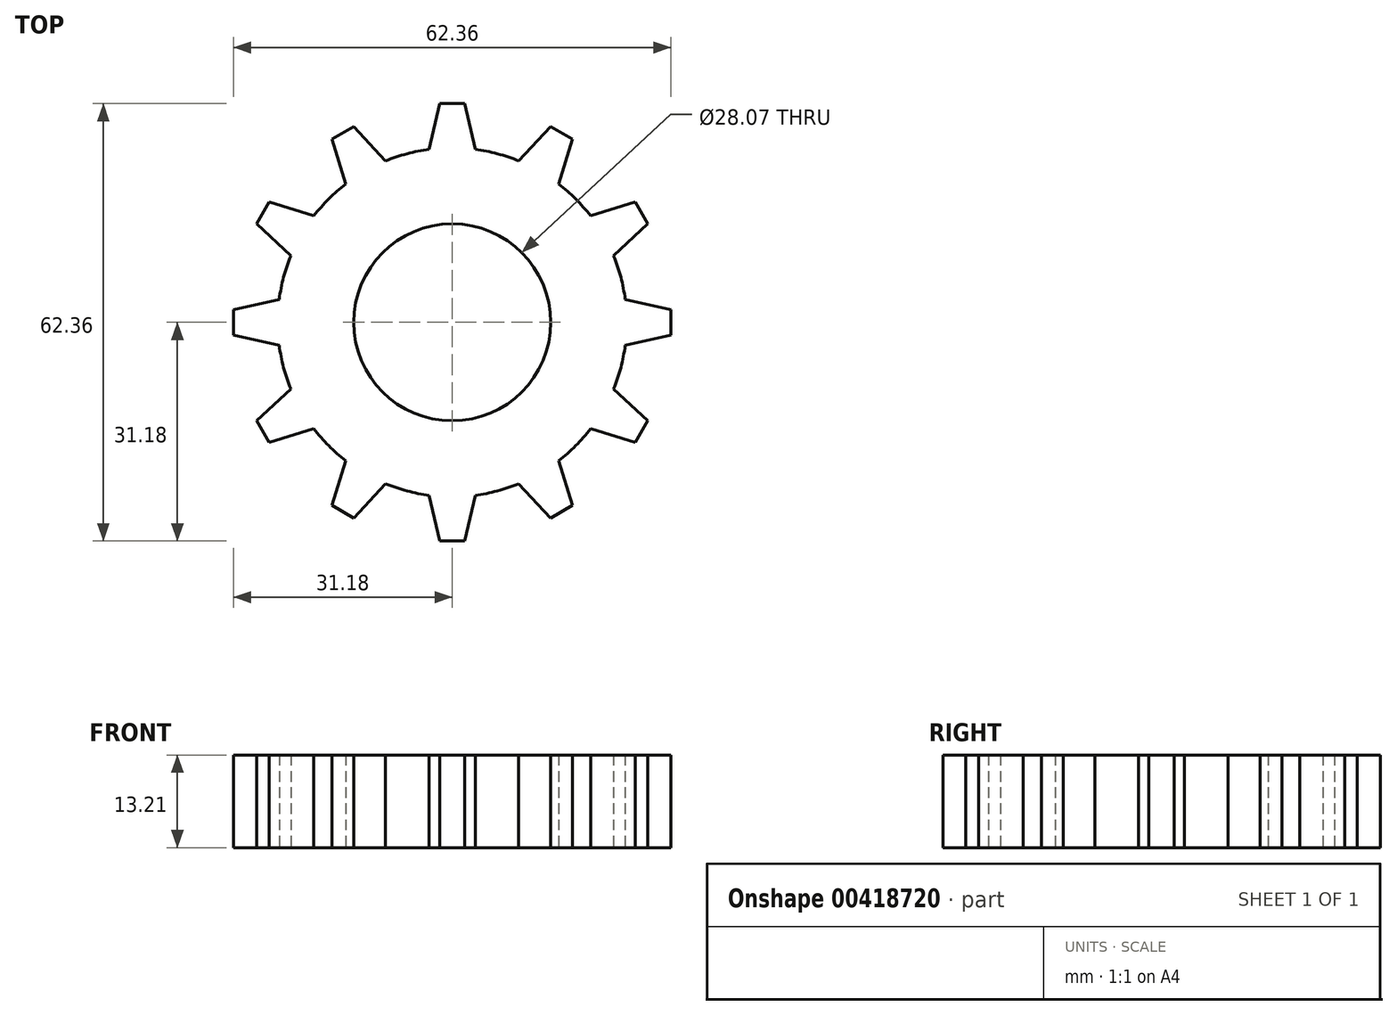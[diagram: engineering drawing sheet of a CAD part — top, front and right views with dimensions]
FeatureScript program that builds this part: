
annotation { "Feature Type Name" : "Feature", "Feature Type Description" : "" }
export const myFeature = defineFeature(function(context is Context, id is Id, definition is map)
    precondition{}
    {
        {
            var Q0;
            Q0=qCreatedBy(makeId("Top.planeOp"),FACE);
            var sketch = newSketch(context, id + "F0", { "sketchPlane" : qUnion([Q0])});
            skCircle(sketch, "E0", {"center": v(0, 0) * mm, "radius": 24.88 * mm});
            skLineSegment(sketch, "E1", {"start": v(0, 24.88) * mm, "end": v(0, 31.18) * mm, "construction": true});
            skLineSegment(sketch, "E2", {"start": v(0, 31.18) * mm, "end": v(-1.8, 31.18) * mm});
            skLineSegment(sketch, "E3", {"start": v(-1.8, 31.18) * mm, "end": v(-3.28, 24.67) * mm});
            skLineSegment(sketch, "E4.MirrorCS", {"start": v(1.8, 31.18) * mm, "end": v(3.28, 24.67) * mm});
            skLineSegment(sketch, "E5.MirrorCS", {"start": v(0, 31.18) * mm, "end": v(1.8, 31.18) * mm});
            skLineSegment(sketch, "E6.1.0", {"start": v(-17.15, 26.1) * mm, "end": v(-15.17, 19.72) * mm});
            skLineSegment(sketch, "E6.1.1", {"start": v(-15.59, 27) * mm, "end": v(-17.15, 26.1) * mm});
            skLineSegment(sketch, "E6.1.2", {"start": v(-15.59, 27) * mm, "end": v(-14.03, 27.9) * mm});
            skLineSegment(sketch, "E6.1.3", {"start": v(-14.03, 27.9) * mm, "end": v(-9.5, 23) * mm});
            skLineSegment(sketch, "E6.2.0", {"start": v(-27.9, 14.03) * mm, "end": v(-23, 9.5) * mm});
            skLineSegment(sketch, "E6.2.1", {"start": v(-27, 15.59) * mm, "end": v(-27.9, 14.03) * mm});
            skLineSegment(sketch, "E6.2.2", {"start": v(-27, 15.59) * mm, "end": v(-26.1, 17.15) * mm});
            skLineSegment(sketch, "E6.2.3", {"start": v(-26.1, 17.15) * mm, "end": v(-19.72, 15.17) * mm});
            skLineSegment(sketch, "E6.3.0", {"start": v(-31.18, -1.8) * mm, "end": v(-24.67, -3.28) * mm});
            skLineSegment(sketch, "E6.3.1", {"start": v(-31.18, 0) * mm, "end": v(-31.18, -1.8) * mm});
            skLineSegment(sketch, "E6.3.2", {"start": v(-31.18, 0) * mm, "end": v(-31.18, 1.8) * mm});
            skLineSegment(sketch, "E6.3.3", {"start": v(-31.18, 1.8) * mm, "end": v(-24.67, 3.28) * mm});
            skLineSegment(sketch, "E6.4.0", {"start": v(-26.1, -17.15) * mm, "end": v(-19.72, -15.17) * mm});
            skLineSegment(sketch, "E6.4.1", {"start": v(-27, -15.59) * mm, "end": v(-26.1, -17.15) * mm});
            skLineSegment(sketch, "E6.4.2", {"start": v(-27, -15.59) * mm, "end": v(-27.9, -14.03) * mm});
            skLineSegment(sketch, "E6.4.3", {"start": v(-27.9, -14.03) * mm, "end": v(-23, -9.5) * mm});
            skLineSegment(sketch, "E6.5.0", {"start": v(-14.03, -27.9) * mm, "end": v(-9.5, -23) * mm});
            skLineSegment(sketch, "E6.5.1", {"start": v(-15.59, -27) * mm, "end": v(-14.03, -27.9) * mm});
            skLineSegment(sketch, "E6.5.2", {"start": v(-15.59, -27) * mm, "end": v(-17.15, -26.1) * mm});
            skLineSegment(sketch, "E6.5.3", {"start": v(-17.15, -26.1) * mm, "end": v(-15.17, -19.72) * mm});
            skLineSegment(sketch, "E6.6.0", {"start": v(1.8, -31.18) * mm, "end": v(3.28, -24.67) * mm});
            skLineSegment(sketch, "E6.6.1", {"start": v(0, -31.18) * mm, "end": v(1.8, -31.18) * mm});
            skLineSegment(sketch, "E6.6.2", {"start": v(0, -31.18) * mm, "end": v(-1.8, -31.18) * mm});
            skLineSegment(sketch, "E6.6.3", {"start": v(-1.8, -31.18) * mm, "end": v(-3.28, -24.67) * mm});
            skLineSegment(sketch, "E6.7.0", {"start": v(17.15, -26.1) * mm, "end": v(15.17, -19.72) * mm});
            skLineSegment(sketch, "E6.7.1", {"start": v(15.59, -27) * mm, "end": v(17.15, -26.1) * mm});
            skLineSegment(sketch, "E6.7.2", {"start": v(15.59, -27) * mm, "end": v(14.03, -27.9) * mm});
            skLineSegment(sketch, "E6.7.3", {"start": v(14.03, -27.9) * mm, "end": v(9.5, -23) * mm});
            skLineSegment(sketch, "E6.8.0", {"start": v(27.9, -14.03) * mm, "end": v(23, -9.5) * mm});
            skLineSegment(sketch, "E6.8.1", {"start": v(27, -15.59) * mm, "end": v(27.9, -14.03) * mm});
            skLineSegment(sketch, "E6.8.2", {"start": v(27, -15.59) * mm, "end": v(26.1, -17.15) * mm});
            skLineSegment(sketch, "E6.8.3", {"start": v(26.1, -17.15) * mm, "end": v(19.72, -15.17) * mm});
            skLineSegment(sketch, "E6.9.0", {"start": v(31.18, 1.8) * mm, "end": v(24.67, 3.28) * mm});
            skLineSegment(sketch, "E6.9.1", {"start": v(31.18, 0) * mm, "end": v(31.18, 1.8) * mm});
            skLineSegment(sketch, "E6.9.2", {"start": v(31.18, 0) * mm, "end": v(31.18, -1.8) * mm});
            skLineSegment(sketch, "E6.9.3", {"start": v(31.18, -1.8) * mm, "end": v(24.67, -3.28) * mm});
            skLineSegment(sketch, "E6.10.0", {"start": v(26.1, 17.15) * mm, "end": v(19.72, 15.17) * mm});
            skLineSegment(sketch, "E6.10.1", {"start": v(27, 15.59) * mm, "end": v(26.1, 17.15) * mm});
            skLineSegment(sketch, "E6.10.2", {"start": v(27, 15.59) * mm, "end": v(27.9, 14.03) * mm});
            skLineSegment(sketch, "E6.10.3", {"start": v(27.9, 14.03) * mm, "end": v(23, 9.5) * mm});
            skLineSegment(sketch, "E6.11.0", {"start": v(14.03, 27.9) * mm, "end": v(9.5, 23) * mm});
            skLineSegment(sketch, "E6.11.1", {"start": v(15.59, 27) * mm, "end": v(14.03, 27.9) * mm});
            skLineSegment(sketch, "E6.11.2", {"start": v(15.59, 27) * mm, "end": v(17.15, 26.1) * mm});
            skLineSegment(sketch, "E6.11.3", {"start": v(17.15, 26.1) * mm, "end": v(15.17, 19.72) * mm});
            skCircle(sketch, "E7", {"center": v(0, 0) * mm, "radius": 14.04 * mm});
            skCircle(sketch, "E8", {"center": v(0, 0) * mm, "radius": 6.84 * mm});
            skSolve(sketch);
        }
        {
            var Q0;
            Q0 = qSketchRegion(id + "F0", true);
            extrude(context, id + "F1", {"entities" : qUnion([Q0]), "depth" : 13.2 * mm});
        }
    });
